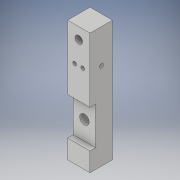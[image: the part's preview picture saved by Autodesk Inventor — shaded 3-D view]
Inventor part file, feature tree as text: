
AUTODESK INVENTOR PART (.ipt)
format: ipt  version: 2018 (Build 220112000, 112)  size: 169,984 bytes
history: native  units: in
note: dims shown in document units (in); Inventor stores cm internally (conversion verified against a paired STEP export)
features: sketch x8, extrude x7, hole x1, thread x1
ambient origin geometry x8: Origin, YZ Plane, XZ Plane, XY Plane, X Axis, Y Axis, Z Axis, Center Point
bodies: Solid1 (feature_tree)
feature tree (17):
  extrude  "Extrusion1"  Depth=4.0in
  extrude  "Extrusion3"  Depth=1.25in
  extrude  "Extrusion4"  Depth=0.74in
  extrude  "Extrusion5"  Depth=0.187in
  extrude  "Extrusion6"  Depth=0.37in
  extrude  "Extrusion7"  Depth=0.25in
  extrude  "Extrusion8"  Depth=0.37in
  hole  "Hole1"  [1 undecoded]
  thread  "Thread1"  [1 undecoded]
  sketch  "Sketch1"  dims[d0=0.74in d1=4.0in]
  sketch  "Sketch2"  dims[d2=0.74in d3=0.0in d4=1.25in]
  sketch  "Sketch3"  dims[d5=0.625in d6=0.74in]
  sketch  "Sketch4"  dims[d9=0.187in d10=0.0in d11=0.312in]
  sketch  "Sketch5"  dims[d12=0.625in d13=0.37in]
  sketch  "Sketch6"  dims[d14=0.6in d15=0.0in d16=0.25in]
  sketch  "Sketch7"  dims[d17=0.375in d18=0.37in]
  sketch  "Sketch9"  dims[d19=0.8in d20=0.0in d21=0.125in d22=0.125in d23=1.125in d24=1.125in d25=0.0687in d26=0.0687in d27=0.8in d28=0.0in d29=0.125in d31=0.0687in d32=1.125in d33=0.437in d34=0.0in d35=0.125in d36=0.365in d37=1.125in d38=0.3in d39=0.0in d43=0.25in d44=0.75in d45=0.375in d46=0.25in d47=0.5635in d48=0.75in d49=0.8108in d50=1.0in d51=0.0in]
note: 2 required parameter values undecoded (feature->parameter linkage not recoverable at this tier; creation-order binding heuristic only, values carry confidence <= 0.55)
